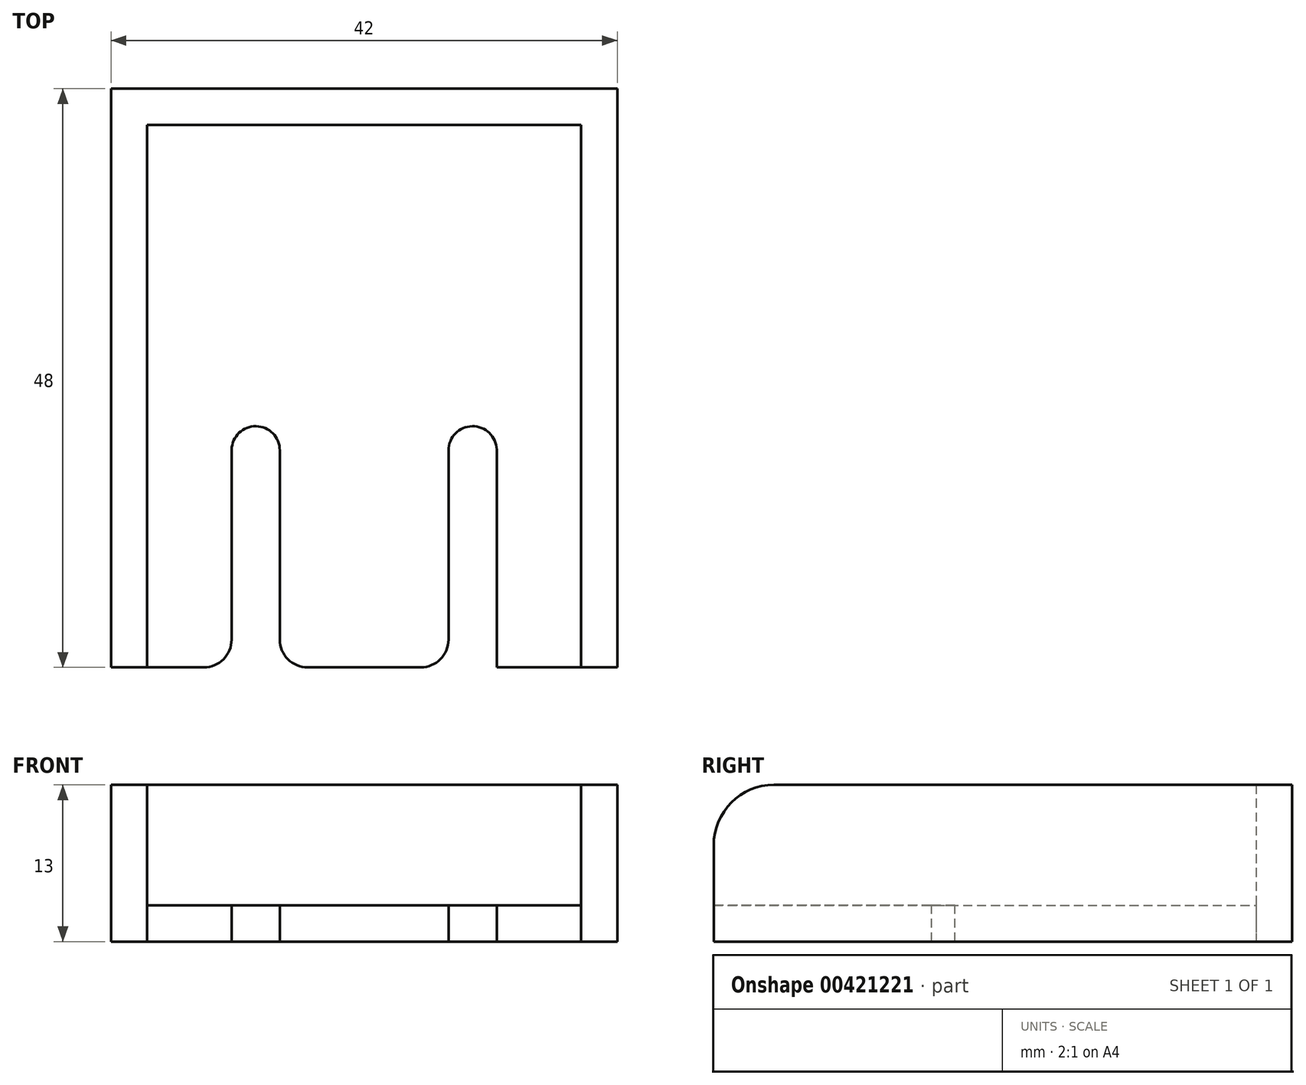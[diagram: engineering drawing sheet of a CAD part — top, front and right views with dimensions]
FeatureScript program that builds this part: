
annotation { "Feature Type Name" : "Feature", "Feature Type Description" : "" }
export const myFeature = defineFeature(function(context is Context, id is Id, definition is map)
    precondition{}
    {
        {
            var Q0;
            Q0=qCreatedBy(makeId("Top.planeOp"),FACE);
            var sketch = newSketch(context, id + "F0", { "sketchPlane" : qUnion([Q0])});
            skLineSegment(sketch, "E0.bottom", {"start": v(18, -22.5) * mm, "end": v(-18, -22.5) * mm});
            skLineSegment(sketch, "E0.top", {"start": v(18, 22.5) * mm, "end": v(-18, 22.5) * mm});
            skLineSegment(sketch, "E0.left", {"start": v(18, -22.5) * mm, "end": v(18, 22.5) * mm});
            skLineSegment(sketch, "E0.right", {"start": v(-18, -22.5) * mm, "end": v(-18, 22.5) * mm});
            skPoint(sketch, "E0.middle", {"position": v(0, 0) * mm});
            skSolve(sketch);
        }
        {
            var Q0;
            Q0 = qSketchRegion(id + "F0", true);
            extrude(context, id + "F1", {"entities" : qUnion([Q0]), "depth" : 3 * mm});
        }
        {
            var Q0;
            Q0=makeQuery(id+"F1.opExtrude","CAP_FACE",FACE,{"disambiguationData":[OSD([sQuery(id+"F0.wireOp",EDGE,"E0.bottom"),sQuery(id+"F0.wireOp",EDGE,"E0.top"),sQuery(id+"F0.wireOp",EDGE,"E0.left"),sQuery(id+"F0.wireOp",EDGE,"E0.right")])],"isStart":false});
            var sketch = newSketch(context, id + "F2", { "sketchPlane" : qUnion([Q0])});
            skArc(sketch, "E1", {"start": v(-7, -4.5) * mm, "mid": v(-9.03, -2.5) * mm, "end": v(-11, -4.57) * mm});
            skLineSegment(sketch, "E2", {"start": v(-11, -4.43) * mm, "end": v(-11, -22.5) * mm});
            skLineSegment(sketch, "E3", {"start": v(-7, -4.5) * mm, "end": v(-7, -22.5) * mm});
            skLineSegment(sketch, "E4.MirrorCS", {"start": v(7, -4.5) * mm, "end": v(7, -22.5) * mm});
            skArc(sketch, "E5.MirrorCS", {"start": v(7, -4.5) * mm, "mid": v(9.03, -2.5) * mm, "end": v(11, -4.57) * mm});
            skLineSegment(sketch, "E6.MirrorCS", {"start": v(11, -4.43) * mm, "end": v(11, -22.5) * mm});
            skSolve(sketch);
        }
        {
            var Q0;
            {var subQ0=sQuery(id+"F2.wireOp",EDGE,"E3");Q0=makeQuery(id+"F2.imprint","IMPRINT",FACE,{"disambiguationData":[TD([[makeQuery(id+"F2.imprint","IMPRINT",EDGE,{"derivedFrom":subQ0}),-1.0]])]});}
            var Q1;
            {var subQ6=sQuery(id+"F2.wireOp",EDGE,"E4.MirrorCS");Q1=makeQuery(id+"F2.imprint","IMPRINT",FACE,{"disambiguationData":[TD([[makeQuery(id+"F2.imprint","IMPRINT",EDGE,{"derivedFrom":subQ6}),1.0]])]});}
            extrude(context, id + "F3", {"entities" : qUnion([Q0, Q1]), "operationType" : NewBodyOperationType.REMOVE, "oppositeDirection" : true, "depth" : 3 * mm});
        }
        {
            var Q0;
            Q0=makeQuery(id+"F1.opExtrude","CAP_FACE",FACE,{"disambiguationData":[OSD([sQuery(id+"F0.wireOp",EDGE,"E0.bottom"),sQuery(id+"F0.wireOp",EDGE,"E0.top"),sQuery(id+"F0.wireOp",EDGE,"E0.left"),sQuery(id+"F0.wireOp",EDGE,"E0.right")])],"isStart":false});
            var sketch = newSketch(context, id + "F4", { "sketchPlane" : qUnion([Q0])});
            skLineSegment(sketch, "E7.0", {"start": v(21, -22.5) * mm, "end": v(21, 25.5) * mm});
            skLineSegment(sketch, "E7.1", {"start": v(21, 25.5) * mm, "end": v(-21, 25.5) * mm});
            skLineSegment(sketch, "E7.2", {"start": v(-21, -22.5) * mm, "end": v(-21, 25.5) * mm});
            skLineSegment(sketch, "E8", {"start": v(-21, -22.5) * mm, "end": v(-18, -22.5) * mm});
            skLineSegment(sketch, "E9", {"start": v(18, -22.5) * mm, "end": v(21, -22.5) * mm});
            skSolve(sketch);
        }
        {
            var Q0;
            Q0=makeQuery(id+"F4.imprint","IMPRINT",FACE,{"disambiguationData":[TD([[makeQuery(id+"F4.imprint","IMPRINT",EDGE,{"derivedFrom":sQuery(id+"F4.wireOp",EDGE,"E7.0")}),1.0]])]});
            extrude(context, id + "F5", {"entities" : qUnion([Q0]), "depth" : 10 * mm, "hasSecondDirection" : true, "secondDirectionOppositeDirection" : true, "secondDirectionDepth" : 3 * mm});
        }
        {
            var Q0;
            Q0=makeQuery(id+"F3.boolean.opBoolean","COPY",EDGE,{"derivedFrom":makeQuery(id+"F3.opExtrude","SWEPT_EDGE",EDGE,{"disambiguationData":[OSD([sQuery(id+"F0.wireOp",EDGE,"E0.bottom"),sQuery(id+"F2.wireOp",EDGE,"E2")])]})});
            var Q1;
            Q1=makeQuery(id+"F3.boolean.opBoolean","COPY",EDGE,{"derivedFrom":makeQuery(id+"F3.opExtrude","SWEPT_EDGE",EDGE,{"disambiguationData":[OSD([sQuery(id+"F0.wireOp",EDGE,"E0.bottom"),sQuery(id+"F2.wireOp",EDGE,"E3")])]})});
            var Q2;
            Q2=makeQuery(id+"F3.boolean.opBoolean","COPY",EDGE,{"derivedFrom":makeQuery(id+"F3.opExtrude","SWEPT_EDGE",EDGE,{"disambiguationData":[OSD([sQuery(id+"F0.wireOp",EDGE,"E0.bottom"),sQuery(id+"F2.wireOp",EDGE,"E4.MirrorCS")])]})});
            var Q3;
            Q3=makeQuery(id+"F3.boolean.opBoolean","COPY",EDGE,{"derivedFrom":makeQuery(id+"F3.opExtrude","SWEPT_EDGE",EDGE,{"disambiguationData":[OSD([sQuery(id+"F0.wireOp",EDGE,"E0.bottom"),sQuery(id+"F2.wireOp",EDGE,"E6.MirrorCS")])]})});
            fillet(context, id + "F6", {"entities" : qUnion([Q0, Q1, Q2, Q3]), "radius" : 2.3 * mm, "tangentPropagation" : true, "allowEdgeOverflow" : false});
        }
        {
            var Q0;
            Q0=makeQuery(id+"F5.opExtrude","CAP_EDGE",EDGE,{"disambiguationData":[OSD([sQuery(id+"F4.wireOp",EDGE,"E8")])],"isStart":false});
            var Q1;
            Q1=makeQuery(id+"F5.opExtrude","CAP_EDGE",EDGE,{"disambiguationData":[OSD([sQuery(id+"F4.wireOp",EDGE,"E9")])],"isStart":false});
            fillet(context, id + "F7", {"entities" : qUnion([Q0, Q1]), "radius" : 5 * mm, "tangentPropagation" : true, "allowEdgeOverflow" : false});
        }
    });
